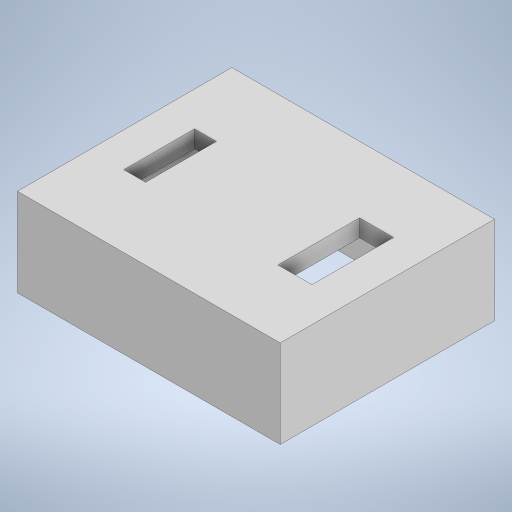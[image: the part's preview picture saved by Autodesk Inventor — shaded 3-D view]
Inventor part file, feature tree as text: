
AUTODESK INVENTOR PART (.ipt)
format: ipt  version: 2024 (Build 280153000, 153)  size: 232,448 bytes
history: native  units: in
note: dims shown in document units (in); Inventor stores cm internally (conversion verified against a paired STEP export)
features: extrude x2, sketch x2, projected_geometry x1
ambient origin geometry x8: Origin, YZ Plane, XZ Plane, XY Plane, X Axis, Y Axis, Z Axis, Center Point
bodies: Solid1 (feature_tree)
feature tree (5):
  extrude  "Extrusion1"  Depth=1.3in
  extrude  "Extrusion2"  Depth=0.6364in
  sketch  "Sketch1"  dims[d0=1.65in d1=1.3in]
  sketch  "Sketch2"  dims[d2=0.2825in d3=0.2559in d4=0.1575in d5=0.5118in d6=0.3711in d7=0.2953in d8=0.2461in d9=0.5906in d10=0.125in d11=0.0in d12=0.125in d13=0.6364in d14=0.0in]
  projected_geometry  "Projected Loop1"
